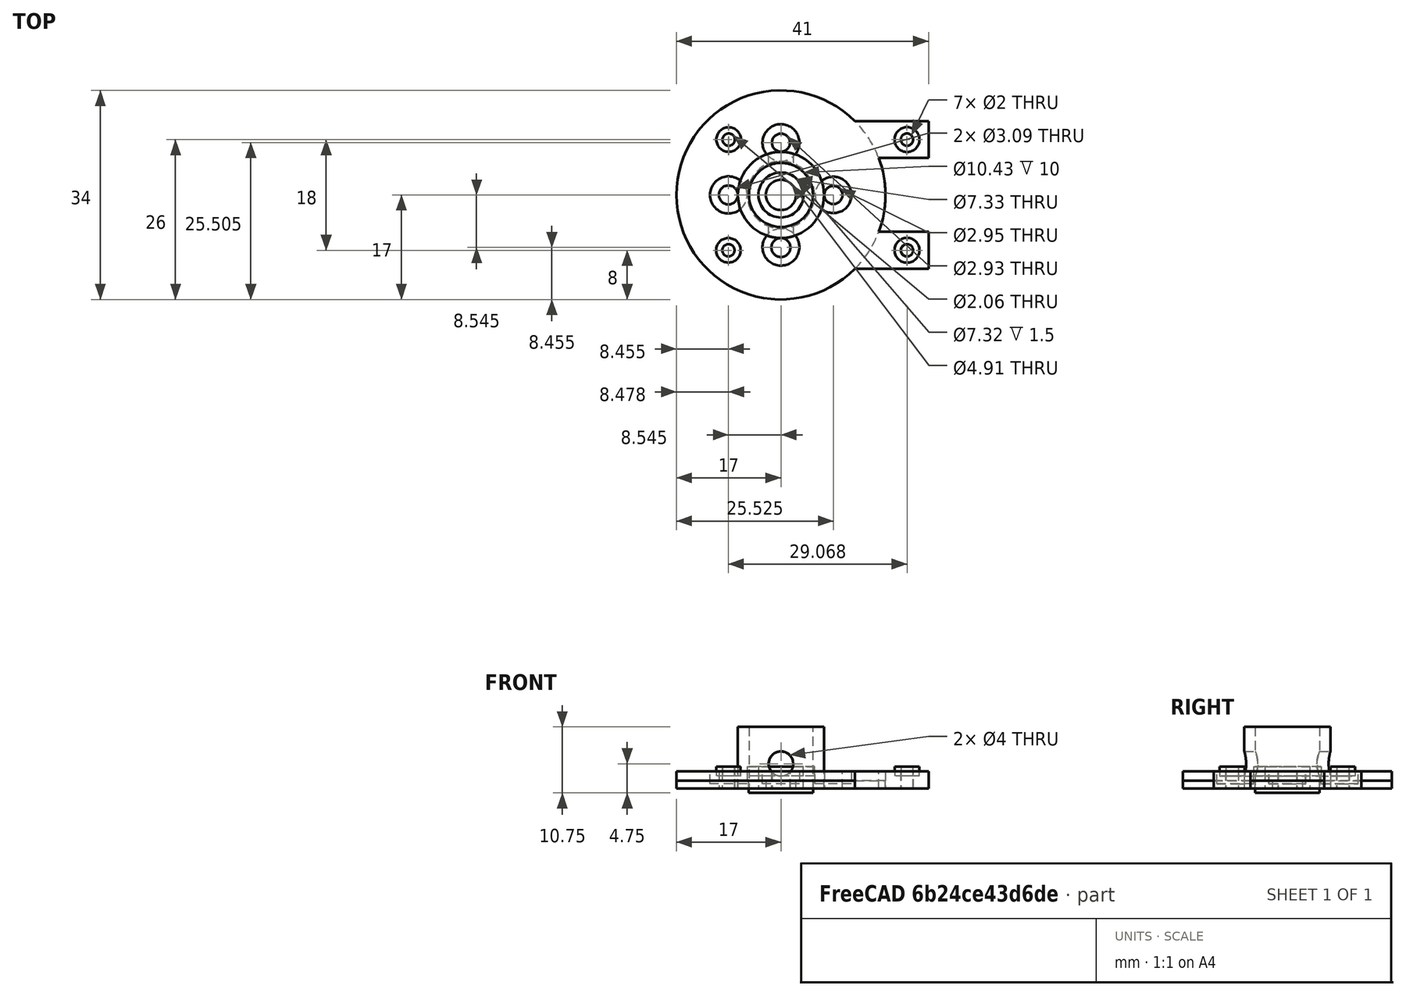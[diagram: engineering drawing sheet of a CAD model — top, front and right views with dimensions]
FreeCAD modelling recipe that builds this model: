
FCSTD DOCUMENT  (FreeCAD 0.14R3703 (Git))
Label: encoderMount
License: CC-BY 3.0
LicenseURL: http://creativecommons.org/licenses/by/3.0/
objects: Sketcher::SketchObject×7, PartDesign::Pad×5, PartDesign::Pocket×2, Part::Cut×1
note: 22 computed .brp shape members not serialized (recipe doc carries the construction recipe); baked Part::Feature solids carry a one-line shape summary decoded from their .brp

FEATURE [Sketcher::SketchObject] Sketch  label="axleMountSketch"
  sketch-geometry (17):
    g0: Circle CenterX=0 CenterY=0 CenterZ=0 NormalX=0 NormalY=0 NormalZ=1 Radius=3.66682
    g1: Circle CenterX=0 CenterY=8.50454 CenterZ=0 NormalX=0 NormalY=0 NormalZ=1 Radius=1.46686
    g2: Circle CenterX=8.52477 CenterY=0 CenterZ=0 NormalX=0 NormalY=0 NormalZ=1 Radius=1.47524
    g3: Circle CenterX=0 CenterY=-8.54499 CenterZ=0 NormalX=0 NormalY=0 NormalZ=1 Radius=1.54499
    g4: Circle CenterX=-8.54499 CenterY=0 CenterZ=0 NormalX=0 NormalY=0 NormalZ=1 Radius=1.54499
    g5: Circle CenterX=-8.52237 CenterY=9 CenterZ=0 NormalX=0 NormalY=0 NormalZ=1 Radius=1.03249
    g6: Circle CenterX=-8.54489 CenterY=-9 CenterZ=0 NormalX=0 NormalY=0 NormalZ=1 Radius=1
    g7: Circle CenterX=20.4785 CenterY=9 CenterZ=0 NormalX=0 NormalY=0 NormalZ=1 Radius=1
    g8: Circle CenterX=20.5235 CenterY=-9 CenterZ=0 NormalX=0 NormalY=0 NormalZ=1 Radius=1
    g9: ArcOfCircle CenterX=0 CenterY=0 CenterZ=0 NormalX=0 NormalY=0 NormalZ=1 Radius=17 StartAngle=0.783668 EndAngle=5.49952
    g10: ArcOfCircle CenterX=0 CenterY=0 CenterZ=0 NormalX=0 NormalY=0 NormalZ=1 Radius=17 StartAngle=5.92247 EndAngle=6.6439
    g11: LineSegment StartX=12.0416 StartY=12 StartZ=0 EndX=24 EndY=12 EndZ=0
    g12: LineSegment StartX=24 StartY=12 StartZ=0 EndX=24 EndY=6 EndZ=0
    g13: LineSegment StartX=24 StartY=6 StartZ=0 EndX=15.906 EndY=6 EndZ=0
    g14: LineSegment StartX=15.906 StartY=-6 StartZ=0 EndX=24 EndY=-6 EndZ=0
    g15: LineSegment StartX=24 StartY=-6 StartZ=0 EndX=24 EndY=-12 EndZ=0
    g16: LineSegment StartX=24 StartY=-12 StartZ=0 EndX=12.0416 EndY=-12 EndZ=0
  constraints (20):
    c: Coincident(g9,g-1)
    c: Radius(g9) = 17
    c: Radius(g7) = 1
    c: Radius(g8) = 1
    c: Equal(g9,g10)
    c: Coincident(g9,g10)
    c: Coincident(g11,g12)
    c: Coincident(g12,g13)
    c: Horizontal(g11)
    c: Horizontal(g13)
    c: Vertical(g12)
    c: Coincident(g14,g15)
    c: Coincident(g15,g16)
    c: Horizontal(g14)
    c: Horizontal(g16)
    c: Vertical(g15)
    c: Coincident(g10,g13)
    c: Coincident(g9,g11)
    c: Coincident(g10,g14)
    c: Coincident(g16,g9)
FEATURE [PartDesign::Pad] Pad  label="axleMountPad"
  Length = 2.75
  Length2 = 0
  Sketch = -> Sketch
  Type = 0
FEATURE [Sketcher::SketchObject] Sketch001  label="standOffsSketch"
  Placement = pos=(0,0,2) rot=(0,0,1;0rad)
  sketch-geometry (10):
    g0: Circle CenterX=-8.49986 CenterY=9 CenterZ=0 NormalX=0 NormalY=0 NormalZ=1 Radius=2
    g1: Circle CenterX=-8.54489 CenterY=-9 CenterZ=0 NormalX=0 NormalY=0 NormalZ=1 Radius=2
    g2: Circle CenterX=20.501 CenterY=9 CenterZ=0 NormalX=0 NormalY=0 NormalZ=1 Radius=1
    g3: Circle CenterX=20.501 CenterY=-9 CenterZ=0 NormalX=0 NormalY=0 NormalZ=1 Radius=1
    g4: Circle CenterX=-8.49986 CenterY=9 CenterZ=0 NormalX=0 NormalY=0 NormalZ=1 Radius=1
    g5: Circle CenterX=-8.54489 CenterY=-9 CenterZ=0 NormalX=0 NormalY=0 NormalZ=1 Radius=1
    g6: Circle CenterX=20.501 CenterY=9 CenterZ=0 NormalX=0 NormalY=0 NormalZ=1 Radius=2.02075
    g7: Circle CenterX=20.501 CenterY=-9 CenterZ=0 NormalX=0 NormalY=0 NormalZ=1 Radius=2.02075
    g8: Circle CenterX=0 CenterY=0 CenterZ=0 NormalX=0 NormalY=0 NormalZ=1 Radius=5.48269
    g9: Circle CenterX=0 CenterY=0 CenterZ=0 NormalX=0 NormalY=0 NormalZ=1 Radius=3.65888
  constraints (4):
    c: Coincident(g4,g0)
    c: Coincident(g5,g1)
    c: Coincident(g6,g2)
    c: Coincident(g7,g3)
FEATURE [PartDesign::Pad] Pad001  label="standOffsPad"
  Length = 1.5
  Length2 = 0
  Placement = pos=(0,0,2) rot=(0,0,1;0rad)
  Sketch = -> Sketch001
  Type = 0
FEATURE [Sketcher::SketchObject] Sketch002
  sketch-geometry (2):
    g0: Circle CenterX=0 CenterY=0 CenterZ=0 NormalX=0 NormalY=0 NormalZ=1 Radius=5.21382
    g1: Circle CenterX=0 CenterY=0 CenterZ=0 NormalX=0 NormalY=0 NormalZ=1 Radius=7
FEATURE [PartDesign::Pad] Pad002  label="wheelHubMount"
  Length = 10
  Length2 = 0
  Sketch = -> Sketch002
  Type = 0
FEATURE [Sketcher::SketchObject] Sketch003
  sketch-geometry (2):
    g0: Circle CenterX=0 CenterY=0 CenterZ=0 NormalX=0 NormalY=0 NormalZ=1 Radius=2.45731
    g1: Circle CenterX=0 CenterY=0 CenterZ=0 NormalX=0 NormalY=0 NormalZ=1 Radius=17
FEATURE [PartDesign::Pad] Pad003  label="encoderWheelSurface"
  Length = 1.25
  Length2 = 0
  Sketch = -> Sketch003
  Type = 0
FEATURE [Sketcher::SketchObject] Sketch004
  Placement = pos=(0,10,0) rot=(-1,0,0;4.71239rad)
  sketch-geometry (1):
    g0: Circle CenterX=0 CenterY=4 CenterZ=0 NormalX=0 NormalY=0 NormalZ=1 Radius=2
FEATURE [PartDesign::Pad] Pad004  label="cylinderForHole"
  Length = 20
  Length2 = 0
  Placement = pos=(0,10,0) rot=(-1,0,0;4.71239rad)
  Sketch = -> Sketch004
  Type = 0
FEATURE [Sketcher::SketchObject] Sketch005
  Placement = pos=(0,0,1.25) rot=(0,0,1;0rad)
  Support = -> Pad003 [Face4]
  sketch-geometry (1):
    g0: Circle CenterX=0 CenterY=0 CenterZ=0 NormalX=0 NormalY=0 NormalZ=1 Radius=5.2186
FEATURE [PartDesign::Pocket] Pocket  label="FINALencoderWheelSurface"
  Length = 2
  Sketch = -> Sketch005
  Type = 0
FEATURE [Part::Cut] Cut  label="FINALaxleMountWithHole"
  Base = -> Pad002
  Tool = -> Pad004
FEATURE [Sketcher::SketchObject] Sketch006  label="mountInsets"
  Placement = pos=(0,0,2.75) rot=(0,0,1;0rad)
  Support = -> Pad [Face19]
  sketch-geometry (4):
    g0: Circle CenterX=0 CenterY=8.50454 CenterZ=0 NormalX=0 NormalY=0 NormalZ=1 Radius=3.00028
    g1: Circle CenterX=-8.52356 CenterY=0 CenterZ=0 NormalX=0 NormalY=0 NormalZ=1 Radius=3.01719
    g2: Circle CenterX=8.52356 CenterY=0 CenterZ=0 NormalX=0 NormalY=0 NormalZ=1 Radius=2.95684
    g3: Circle CenterX=0 CenterY=-8.49339 CenterZ=0 NormalX=0 NormalY=0 NormalZ=1 Radius=3
FEATURE [PartDesign::Pocket] Pocket001  label="FINALencoderChassisMount"
  Length = 2
  Sketch = -> Sketch006
  Type = 0
